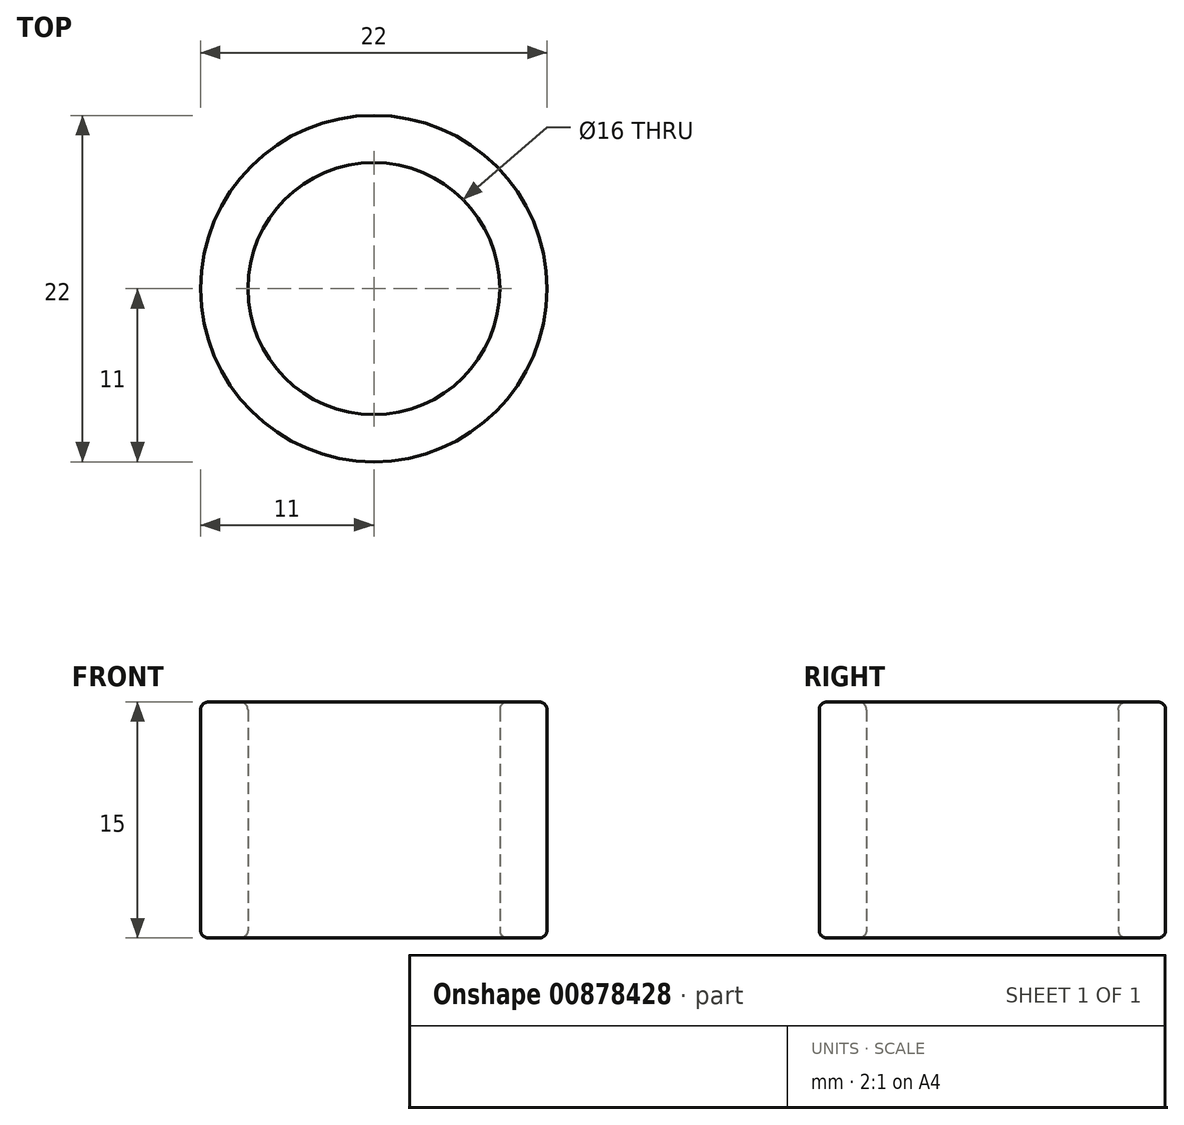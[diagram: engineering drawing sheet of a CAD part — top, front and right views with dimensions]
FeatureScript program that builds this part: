
annotation { "Feature Type Name" : "Feature", "Feature Type Description" : "" }
export const myFeature = defineFeature(function(context is Context, id is Id, definition is map)
    precondition{}
    {
        {
            var Q0;
            Q0=qCreatedBy(makeId("Top.planeOp"),FACE);
            var sketch = newSketch(context, id + "F0", { "sketchPlane" : qUnion([Q0])});
            skCircle(sketch, "E0", {"center": v(0, 0) * mm, "radius": 11 * mm});
            skCircle(sketch, "E1", {"center": v(0, 0) * mm, "radius": 8 * mm});
            skSolve(sketch);
        }
        {
            var Q0;
            Q0=makeQuery(id+"F0.imprint","IMPRINT",FACE,{"disambiguationData":[TD([[makeQuery(id+"F0.imprint","IMPRINT",EDGE,{"derivedFrom":sQuery(id+"F0.wireOp",EDGE,"E0")}),1.0]])]});
            extrude(context, id + "F1", {"entities" : qUnion([Q0]), "depth" : 15 * mm, "offsetDistance" : 25.4 * mm});
        }
        {
            var Q0;
            Q0=makeQuery(id+"F1.opExtrude","CAP_EDGE",EDGE,{"disambiguationData":[OSD([sQuery(id+"F0.wireOp",EDGE,"E0")])],"isStart":false});
            var Q1;
            Q1=makeQuery(id+"F1.opExtrude","CAP_EDGE",EDGE,{"disambiguationData":[OSD([sQuery(id+"F0.wireOp",EDGE,"E0")])],"isStart":true});
            fillet(context, id + "F2", {"entities" : qUnion([Q0, Q1]), "radius" : 0.5 * mm, "tangentPropagation" : true, "allowEdgeOverflow" : false});
        }
        {
            var Q0;
            Q0=makeQuery(id+"F1.opExtrude","CAP_EDGE",EDGE,{"disambiguationData":[OSD([sQuery(id+"F0.wireOp",EDGE,"E1")])],"isStart":false});
            var Q1;
            Q1=makeQuery(id+"F1.opExtrude","CAP_EDGE",EDGE,{"disambiguationData":[OSD([sQuery(id+"F0.wireOp",EDGE,"E1")])],"isStart":true});
            fillet(context, id + "F3", {"entities" : qUnion([Q0, Q1]), "radius" : 0.5 * mm, "tangentPropagation" : true, "allowEdgeOverflow" : false});
        }
    });
